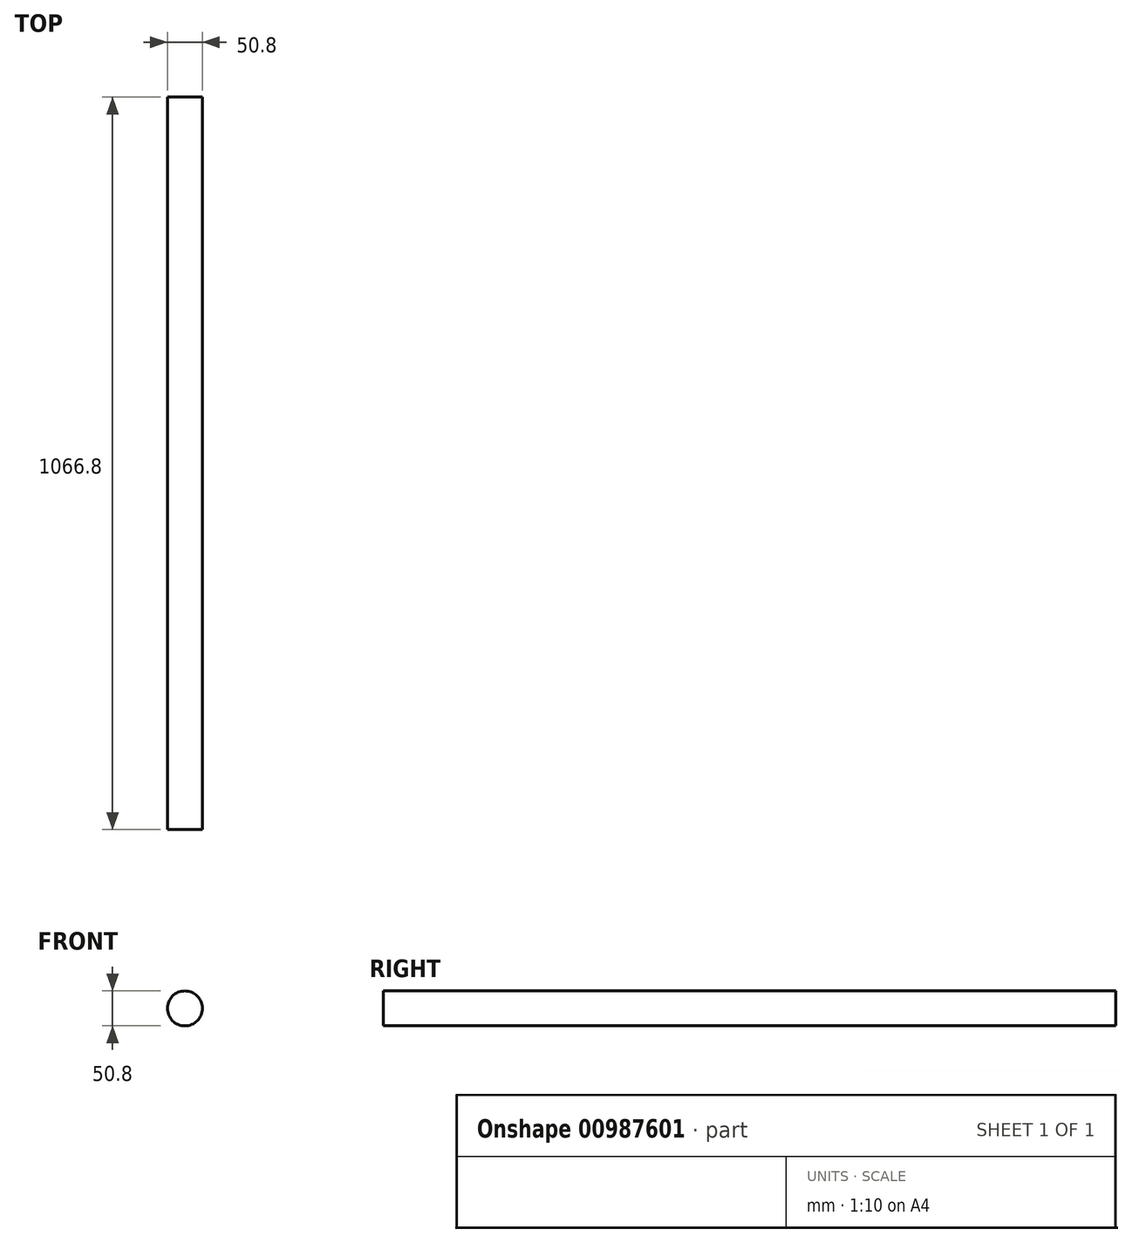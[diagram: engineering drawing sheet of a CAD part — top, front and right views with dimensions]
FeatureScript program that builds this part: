
annotation { "Feature Type Name" : "Feature", "Feature Type Description" : "" }
export const myFeature = defineFeature(function(context is Context, id is Id, definition is map)
    precondition{}
    {
        {
            var Q0;
            Q0=qCreatedBy(makeId("Front.planeOp"),FACE);
            var sketch = newSketch(context, id + "F0", { "sketchPlane" : qUnion([Q0])});
            skCircle(sketch, "E0", {"center": v(-44.05, 31.67) * mm, "radius": 25.4 * mm});
            skSolve(sketch);
        }
        {
            var Q0;
            Q0=qSketchRegion(id+"F0",true);
            extrude(context, id + "F1", {"entities" : qUnion([Q0]), "depth" : 1066.8 * mm, "offsetDistance" : 25.4 * mm});
        }
    });
